# Revit family: Seating-Casual-Naughtone-Cloud_Plain_1_Seat
name_source: partatom
category: Furniture
revit_build: Autodesk Revit 2014 (Build: 20140709_2115(x64)
units: mm (PartAtom-declared; Revit-internal decimal feet)

## types (1)
- CLO-P-1-LO
    Additional Materials = Additional material and finish options available. Please contact Naughtone direct for further information.
    AssetIdentifier = CLO-P-1-LO
    Barcode = 0
    COBie Description = Designed by Naughtone, Cloud plain seating system's tactile, pillowy surround is designed to invite and comfort without consuming masses of space. Whether you are looking for somewhere to shelter or meet or simply to relax, cloud has a magnetic appeal.
    Cost = 0 $
    Current Revision = 1
    Depth = 750 mm
    Description = Cloud Armchair with Low Back
    Height = 650 mm  [stored 2.13255 ft]
    Length = 800 mm  [stored 2.62467 ft]
    Manufacturer = Naughtone
    Model = Cloud Armchair with Low Back
    Name = Furniture-Seating-Casual-Cloud_Plain
    Product Code = CLO-P-1-LO
    Product URL = http://www.naughtone.com
    SerialNumber = 0
    TagNumber = 0
    TypeName = 800mmx750mm650mm, Cloud Plain Seating
    URL = http://www.naughtone.com
    Uniclass = Pr_40_50_12_81
    WarrantyDuration = 60

note: [stored X ft] marks values corroborated as IEEE doubles in the binary element streams (Revit-internal decimal feet)

## geometry (parser evidence)
native form markers: Blend x2, Sweep x7
no freeform markers — native parametric forms only
